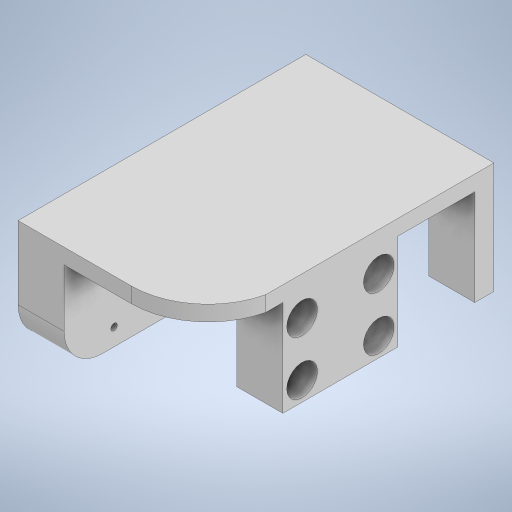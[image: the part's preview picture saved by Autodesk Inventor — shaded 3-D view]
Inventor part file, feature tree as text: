
AUTODESK INVENTOR PART (.ipt)
format: ipt  version: 2024.1 (Build 281209000, 209)  size: 358,912 bytes
history: native  units: mm
features: extrude x9, sketch x9, fillet x2, other x1
ambient origin geometry x8: Origin, YZ Plane, XZ Plane, XY Plane, X Axis, Y Axis, Z Axis, Center Point
bodies: Body1 (feature_tree)
feature tree (21):
  other  "ソリッド1"
  extrude  "押し出し1"  Depth=50.0mm
  extrude  "押し出し2"  Depth=75.0mm
  extrude  "押し出し3"  Depth=29.0mm TaperAngle=0.0deg
  extrude  "押し出し4"  Depth=25.0mm
  extrude  "押し出し5"  Depth=25.0mm TaperAngle=0.0deg
  fillet  "フィレット1"  Radius=20.0mm
  extrude  "押し出し6"  Depth=20.0mm
  fillet  "フィレット2"  Radius=50.0mm
  extrude  "押し出し7"  Depth=29.0mm TaperAngle=0.0deg
  extrude  "押し出し8"  Depth=1.7mm
  extrude  "押し出し9"  Depth=1.7mm
  sketch  "スケッチ1"
  sketch  "スケッチ2"
  sketch  "スケッチ3"
  sketch  "スケッチ4"
  sketch  "スケッチ5"
  sketch  "スケッチ7"
  sketch  "スケッチ8"
  sketch  "スケッチ9"
  sketch  "スケッチ11"
